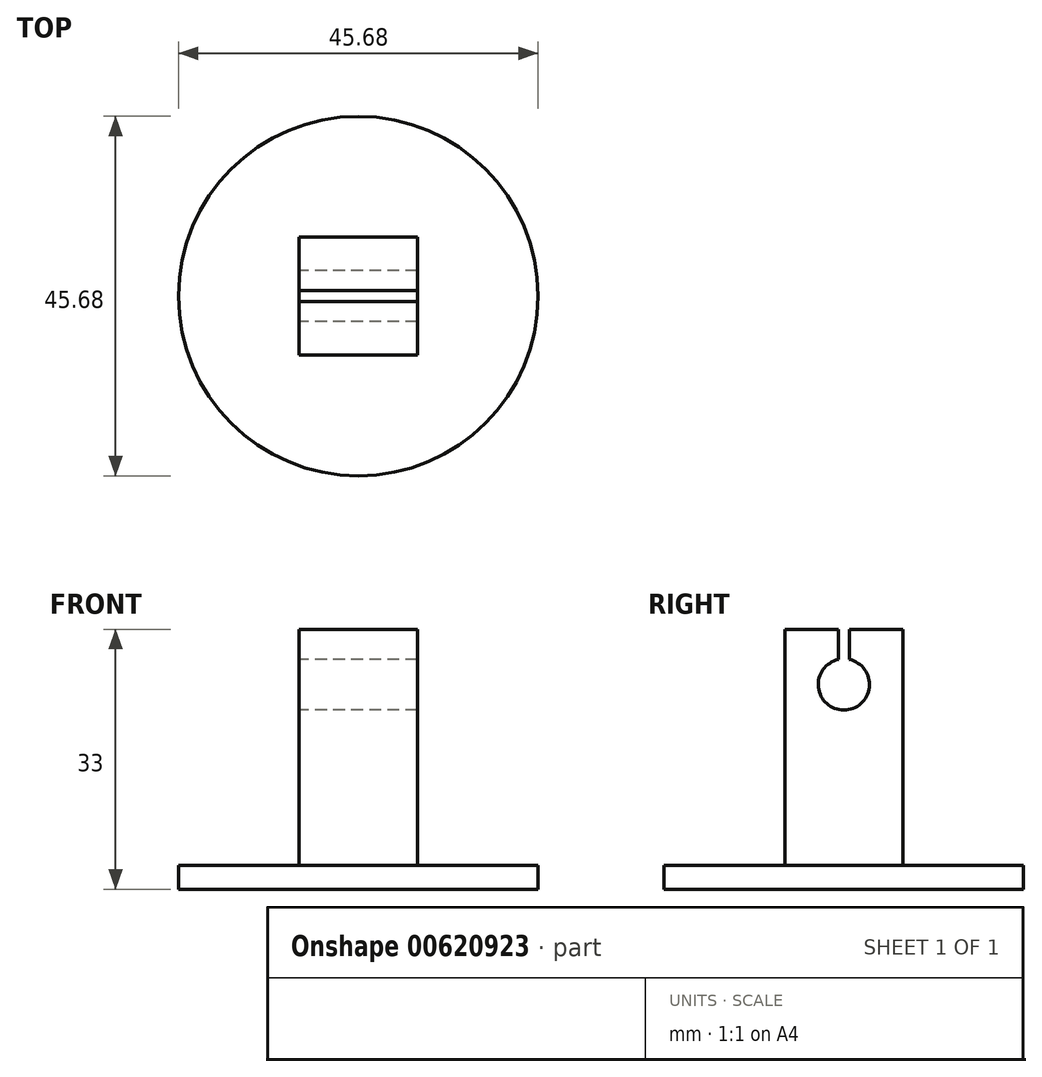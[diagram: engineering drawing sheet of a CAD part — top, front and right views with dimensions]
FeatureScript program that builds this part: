
annotation { "Feature Type Name" : "Feature", "Feature Type Description" : "" }
export const myFeature = defineFeature(function(context is Context, id is Id, definition is map)
    precondition{}
    {
        {
            var Q0;
            Q0=qCreatedBy(makeId("Top.planeOp"),FACE);
            var sketch = newSketch(context, id + "F0", { "sketchPlane" : qUnion([Q0])});
            skCircle(sketch, "E0", {"center": v(0, 0) * mm, "radius": 22.84 * mm});
            skSolve(sketch);
        }
        {
            var Q0;
            Q0=makeQuery(id+"F0.imprint","IMPRINT",FACE,{"disambiguationData":[TD([[makeQuery(id+"F0.imprint","IMPRINT",EDGE,{"derivedFrom":sQuery(id+"F0.wireOp",EDGE,"E0")}),1.0]])]});
            extrude(context, id + "F1", {"entities" : qUnion([Q0]), "depth" : 3 * mm, "offsetDistance" : 25 * mm});
        }
        {
            var Q0;
            Q0=makeQuery(id+"F1.opExtrude","CAP_FACE",FACE,{"disambiguationData":[OSD([sQuery(id+"F0.wireOp",EDGE,"E0")])],"isStart":false});
            var sketch = newSketch(context, id + "F2", { "sketchPlane" : qUnion([Q0])});
            skLineSegment(sketch, "E1.bottom", {"start": v(-7.5, 7.5) * mm, "end": v(7.5, 7.5) * mm});
            skLineSegment(sketch, "E1.top", {"start": v(-7.5, -7.5) * mm, "end": v(7.5, -7.5) * mm});
            skLineSegment(sketch, "E1.left", {"start": v(-7.5, 7.5) * mm, "end": v(-7.5, -7.5) * mm});
            skLineSegment(sketch, "E1.right", {"start": v(7.5, 7.5) * mm, "end": v(7.5, -7.5) * mm});
            skPoint(sketch, "E1.middle", {"position": v(0, 0) * mm});
            skSolve(sketch);
        }
        {
            var Q0;
            Q0=makeQuery(id+"F2.imprint","IMPRINT",FACE,{"disambiguationData":[TD([[makeQuery(id+"F2.imprint","IMPRINT",EDGE,{"derivedFrom":sQuery(id+"F2.wireOp",EDGE,"E1.bottom")}),-1.0]])]});
            extrude(context, id + "F3", {"entities" : qUnion([Q0]), "operationType" : NewBodyOperationType.ADD, "depth" : 30 * mm, "offsetDistance" : 25 * mm});
        }
        {
            var Q0;
            Q0=makeQuery(id+"F3.opExtrude","SWEPT_FACE",FACE,{"disambiguationData":[OSD([sQuery(id+"F2.wireOp",EDGE,"E1.left")])]});
            var sketch = newSketch(context, id + "F4", { "sketchPlane" : qUnion([Q0])});
            skPoint(sketch, "E2.endSnap0", {"position": v(0, 3) * mm});
            skArc(sketch, "E3", {"start": v(-0.7, 29.17) * mm, "mid": v(0, 22.75) * mm, "end": v(0.7, 29.17) * mm});
            skLineSegment(sketch, "E4", {"start": v(-0.7, 33) * mm, "end": v(-0.7, 29.17) * mm});
            skLineSegment(sketch, "E5.MirrorCS", {"start": v(0.7, 33) * mm, "end": v(0.7, 29.17) * mm});
            skSolve(sketch);
        }
        {
            var Q0;
            Q0=makeQuery(id+"F4.imprint","IMPRINT",FACE,{"disambiguationData":[TD([[makeQuery(id+"F4.imprint","IMPRINT",EDGE,{"derivedFrom":sQuery(id+"F4.wireOp",EDGE,"E3")}),1.0]])]});
            extrude(context, id + "F5", {"entities" : qUnion([Q0]), "operationType" : NewBodyOperationType.REMOVE, "oppositeDirection" : true, "depth" : 25 * mm, "offsetDistance" : 25 * mm});
        }
    });
